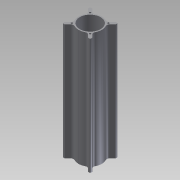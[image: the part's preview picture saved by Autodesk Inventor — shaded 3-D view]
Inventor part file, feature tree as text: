
AUTODESK INVENTOR PART (.ipt)
format: ipt  version: 2012 SP2 (Build 160219200, 219)  size: 130,560 bytes
history: native  units: mm
features: extrude x1, sketch x1
ambient origin geometry x8: Origin, YZ Plane, XZ Plane, XY Plane, X Axis, Y Axis, Z Axis, Center Point
bodies: Solid1 (feature_tree)
feature tree (2):
  extrude  "Extrusion1"  [1 undecoded]
  sketch  "Sketch1"  dims[d0=400.0mm d1=0.0mm]
note: 1 required parameter value undecoded (feature->parameter linkage not recoverable at this tier; creation-order binding heuristic only, values carry confidence <= 0.55)
